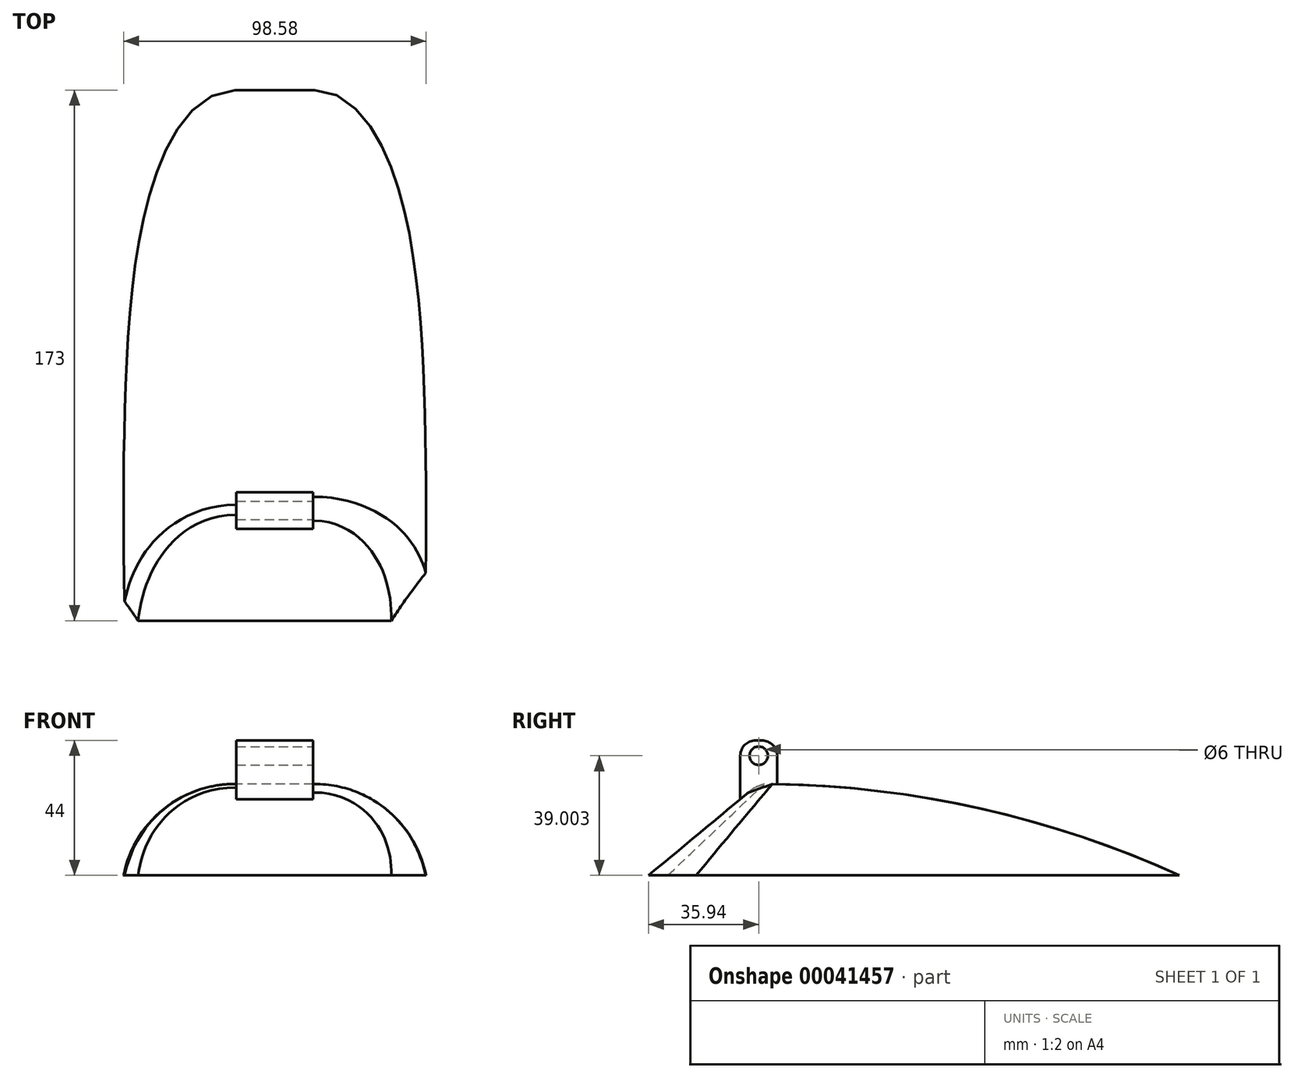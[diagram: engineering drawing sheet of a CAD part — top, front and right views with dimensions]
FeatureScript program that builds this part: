
annotation { "Feature Type Name" : "Feature", "Feature Type Description" : "" }
export const myFeature = defineFeature(function(context is Context, id is Id, definition is map)
    precondition{}
    {
        {
            var Q0;
            Q0=qCreatedBy(makeId("Right.planeOp"),FACE);
            var sketch = newSketch(context, id + "F0", { "sketchPlane" : qUnion([Q0])});
            skArc(sketch, "E0", {"start": v(137.06, 300.2) * mm, "mid": v(70.13, 322.46) * mm, "end": v(0, 330) * mm});
            skLineSegment(sketch, "E1", {"start": v(0, 300.2) * mm, "end": v(137.06, 300.2) * mm});
            skLineSegment(sketch, "E2", {"start": v(0, 330) * mm, "end": v(-35.94, 300.2) * mm});
            skLineSegment(sketch, "E3", {"start": v(0, 300.2) * mm, "end": v(-35.94, 300.2) * mm});
            skSolve(sketch);
        }
        {
            var Q0;
            Q0=makeQuery(id+"F0.imprint","IMPRINT",FACE,{"disambiguationData":[TD([[makeQuery(id+"F0.imprint","IMPRINT",EDGE,{"derivedFrom":sQuery(id+"F0.wireOp",EDGE,"E0")}),1.0]])]});
            extrude(context, id + "F1", {"entities" : qUnion([Q0]), "depth" : 100 * mm});
        }
        {
            var Q0;
            Q0=makeQuery(id+"F1.opExtrude","SWEPT_FACE",FACE,{"disambiguationData":[OSD([sQuery(id+"F0.wireOp",EDGE,"E1"),sQuery(id+"F0.wireOp",EDGE,"E3")])]});
            var sketch = newSketch(context, id + "F2", { "sketchPlane" : qUnion([Q0])});
            skLineSegment(sketch, "E4", {"start": v(50, 35.94) * mm, "end": v(50, -52.47) * mm, "construction": true});
            skLineSegment(sketch, "E5", {"start": v(0, 0) * mm, "end": v(100, 0) * mm, "construction": true});
            skLineSegment(sketch, "E6.rect.bottom", {"start": v(62.5, -6) * mm, "end": v(37.5, -6) * mm});
            skLineSegment(sketch, "E6.rect.top", {"start": v(62.5, 6) * mm, "end": v(37.5, 6) * mm});
            skLineSegment(sketch, "E6.rect.left", {"start": v(62.5, -6) * mm, "end": v(62.5, 6) * mm});
            skLineSegment(sketch, "E6.rect.right", {"start": v(37.5, -6) * mm, "end": v(37.5, 6) * mm});
            skPoint(sketch, "E6.rect.middle", {"position": v(50, 0) * mm});
            skSolve(sketch);
        }
        {
            var Q0;
            Q0 = qSketchRegion(id + "F2", true);
            extrude(context, id + "F3", {"entities" : qUnion([Q0]), "operationType" : NewBodyOperationType.ADD, "oppositeDirection" : true, "depth" : 44 * mm});
        }
        {
            var Q0;
            Q0=makeQuery(id+"F3.opExtrude","CAP_EDGE",EDGE,{"disambiguationData":[OSD([sQuery(id+"F2.wireOp",EDGE,"E6.rect.top")])],"isStart":false});
            var Q1;
            Q1=makeQuery(id+"F3.opExtrude","CAP_EDGE",EDGE,{"disambiguationData":[OSD([sQuery(id+"F2.wireOp",EDGE,"E6.rect.bottom")])],"isStart":false});
            fillet(context, id + "F4", {"entities" : qUnion([Q0, Q1]), "radius" : 5 * mm, "tangentPropagation" : true, "allowEdgeOverflow" : false});
        }
        {
            var Q0;
            Q0=makeQuery(id+"F1.opExtrude","CAP_EDGE",EDGE,{"disambiguationData":[OSD([sQuery(id+"F0.wireOp",EDGE,"E0")])],"isStart":false});
            fillet(context, id + "F5", {"entities" : qUnion([Q0]), "radius" : 37 * mm, "tangentPropagation" : true, "allowEdgeOverflow" : false});
        }
        {
            var Q0;
            Q0=makeQuery(id+"F1.opExtrude","CAP_EDGE",EDGE,{"disambiguationData":[OSD([sQuery(id+"F0.wireOp",EDGE,"E0")])],"isStart":true});
            fillet(context, id + "F6", {"entities" : qUnion([Q0]), "radius" : 37 * mm, "tangentPropagation" : true, "allowEdgeOverflow" : false});
        }
        {
            var Q0;
            Q0=makeQuery(id+"F3.opExtrude","SWEPT_FACE",FACE,{"disambiguationData":[OSD([sQuery(id+"F2.wireOp",EDGE,"E6.rect.left")])]});
            var sketch = newSketch(context, id + "F7", { "sketchPlane" : qUnion([Q0])});
            skPoint(sketch, "E7.endSnap0", {"position": v(0, 344.2) * mm});
            skCircle(sketch, "E8", {"center": v(0, 339.2) * mm, "radius": 3 * mm});
            skPoint(sketch, "E7.start.orphan", {"position": v(0, 344.2) * mm});
            skPoint(sketch, "E9.trimOffspring.end.orphan", {"position": v(0, 334.56) * mm});
            skSolve(sketch);
        }
        {
            var Q0;
            Q0=makeQuery(id+"F7.imprint","IMPRINT",FACE,{"disambiguationData":[TD([[makeQuery(id+"F7.imprint","IMPRINT",EDGE,{"derivedFrom":sQuery(id+"F7.wireOp",EDGE,"E8")}),1.0]])]});
            extrude(context, id + "F8", {"entities" : qUnion([Q0]), "operationType" : NewBodyOperationType.REMOVE, "endBound" : BoundingType.THROUGH_ALL, "oppositeDirection" : true, "depth" : 25 * mm});
        }
        {
            var Q0;
            Q0=makeQuery(id+"F6.opFillet","BLEND_EDGE",EDGE,{"blendedFrom":[makeQuery(id+"F1.opExtrude","CAP_EDGE",EDGE,{"disambiguationData":[OSD([sQuery(id+"F0.wireOp",EDGE,"E0")])],"isStart":true}),makeQuery(id+"F1.opExtrude","SWEPT_FACE",FACE,{"disambiguationData":[OSD([sQuery(id+"F0.wireOp",EDGE,"E2")])]})],"blendedInto":[makeQuery(id+"F1.opExtrude","SWEPT_FACE",FACE,{"disambiguationData":[OSD([sQuery(id+"F0.wireOp",EDGE,"E2")])]})]});
            chamfer(context, id + "F9", {"entities" : qUnion([Q0]), "width" : 5 * mm, "tangentPropagation" : true});
        }
        {
            var Q0;
            Q0=makeQuery(id+"F5.opFillet","BLEND_EDGE",EDGE,{"blendedFrom":[makeQuery(id+"F1.opExtrude","CAP_EDGE",EDGE,{"disambiguationData":[OSD([sQuery(id+"F0.wireOp",EDGE,"E0")])],"isStart":false}),makeQuery(id+"F1.opExtrude","SWEPT_FACE",FACE,{"disambiguationData":[OSD([sQuery(id+"F0.wireOp",EDGE,"E2")])]})],"blendedInto":[makeQuery(id+"F1.opExtrude","SWEPT_FACE",FACE,{"disambiguationData":[OSD([sQuery(id+"F0.wireOp",EDGE,"E2")])]})]});
            chamfer(context, id + "F10", {"entities" : qUnion([Q0]), "width" : 12 * mm, "tangentPropagation" : true});
        }
    });
